# Revit family: Air Terminals_Abmessungen Gewichte DAL359 Anschlusskasten quadratisch
name_source: partatom
category: Air Terminals
revit_build: Autodesk Revit 2017 (Build: 20190508_0315(x64)
units: mm (PartAtom-declared; Revit-internal decimal feet)

## family parameters
Always vertical = Yes
Cut with Voids When Loaded = No
Part Type = Normal
Room Calculation Point = No
Round Connector Dimension = Use Diameter
Shared = No
Work Plane-Based = No

## types (12) — shared parameters
Maß E = 12 mm  [stored 0.0393701 ft]
Product url = https://www.kampmann.de

## per-type parameters (varying)
| type | Index | Material | Maß B | Maß H | Maß Ø D | Maß □ A | Model Type | Right | Top |
| DAL359_300_Air right | 1 | RAL9010 | 170 mm  [stored 0.557743 ft] | 275 mm | 158 mm | 292 mm  [stored 0.958005 ft] | DAL359_300 | Yes | No |
| DAL359_400_Air right | 2 | <By Category> | 190 mm | 315 mm  [stored 1.03346 ft] | 198 mm  [stored 0.649606 ft] | 392 mm  [stored 1.28609 ft] | DAL359_400 | Yes | No |
| DAL359_500_Air right | 3 | <By Category> | 203 mm  [stored 0.66601 ft] | 340 mm  [stored 1.11549 ft] | 222 mm | 492 mm  [stored 1.61417 ft] | DAL359_500 | Yes | No |
| DAL359_600_Air right | 4 | <By Category> | 215 mm | 365 mm  [stored 1.19751 ft] | 248 mm  [stored 0.813648 ft] | 589 mm | DAL359_600 | Yes | No |
| DAL359_625_Air right | 5 | <By Category> | 215 mm | 365 mm  [stored 1.19751 ft] | 248 mm  [stored 0.813648 ft] | 614 mm  [stored 2.01444 ft] | DAL359_625 | Yes | No |
| DAL359_800_Air right | 6 | <By Category> | 248 mm  [stored 0.813648 ft] | 430 mm | 313 mm  [stored 1.0269 ft] | 794 mm  [stored 2.60499 ft] | DAL359_800 | Yes | No |
| DAL359_800_Air top | 6 | <By Category> | 248 mm  [stored 0.813648 ft] | 430 mm | 313 mm  [stored 1.0269 ft] | 794 mm  [stored 2.60499 ft] | DAL359_800 | No | Yes |
| DAL359_625_Air top | 5 | <By Category> | 215 mm | 365 mm  [stored 1.19751 ft] | 248 mm  [stored 0.813648 ft] | 614 mm  [stored 2.01444 ft] | DAL359_625 | No | Yes |
| DAL359_600_Air top | 4 | <By Category> | 215 mm | 365 mm  [stored 1.19751 ft] | 248 mm  [stored 0.813648 ft] | 589 mm | DAL359_600 | No | Yes |
| DAL359_500_Air top | 3 | <By Category> | 203 mm  [stored 0.66601 ft] | 340 mm  [stored 1.11549 ft] | 222 mm | 492 mm  [stored 1.61417 ft] | DAL359_500 | No | Yes |
| DAL359_400_Air top | 2 | <By Category> | 190 mm | 315 mm  [stored 1.03346 ft] | 198 mm  [stored 0.649606 ft] | 392 mm  [stored 1.28609 ft] | DAL359_400 | No | Yes |
| DAL359_300_Air top | 1 | RAL9010 | 170 mm  [stored 0.557743 ft] | 275 mm | 158 mm | 292 mm  [stored 0.958005 ft] | DAL359_300 | No | Yes |

note: [stored X ft] marks values corroborated as IEEE doubles in the binary element streams (Revit-internal decimal feet)

## geometry (parser evidence)
native form markers: Sweep x38
no freeform markers — native parametric forms only
